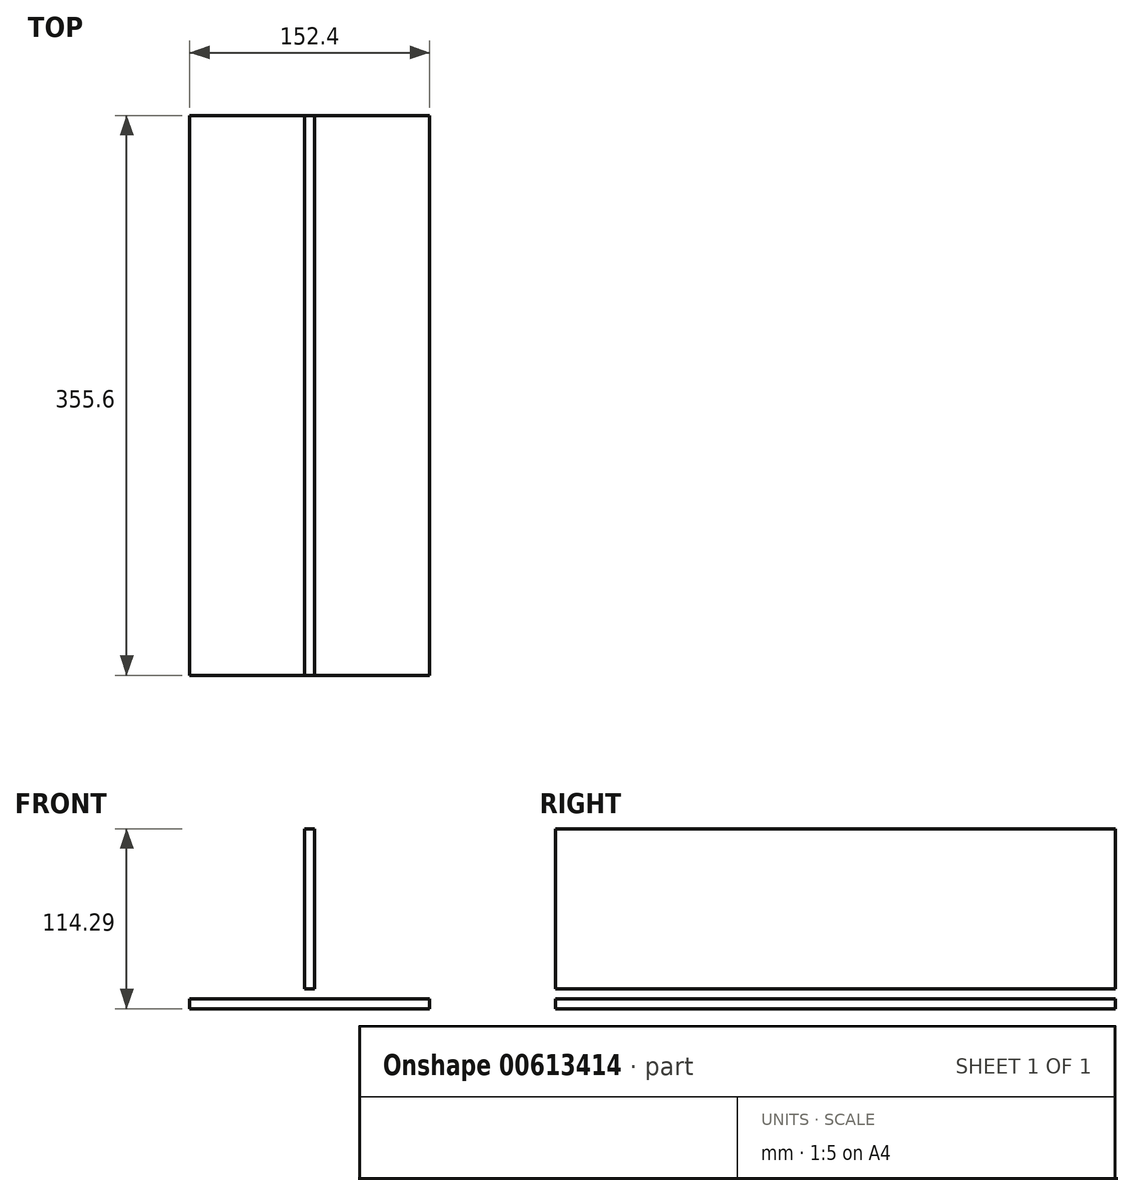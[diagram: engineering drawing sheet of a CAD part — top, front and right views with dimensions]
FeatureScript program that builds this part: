
annotation { "Feature Type Name" : "Feature", "Feature Type Description" : "" }
export const myFeature = defineFeature(function(context is Context, id is Id, definition is map)
    precondition{}
    {
        {
            var Q0;
            Q0=qCreatedBy(makeId("Front.planeOp"),FACE);
            var sketch = newSketch(context, id + "F0", { "sketchPlane" : qUnion([Q0])});
            skLineSegment(sketch, "E0.bottom", {"start": v(-76.2, 3.17) * mm, "end": v(76.2, 3.17) * mm});
            skLineSegment(sketch, "E0.top", {"start": v(-76.2, -3.17) * mm, "end": v(76.2, -3.17) * mm});
            skLineSegment(sketch, "E0.left", {"start": v(-76.2, 3.17) * mm, "end": v(-76.2, -3.17) * mm});
            skLineSegment(sketch, "E0.right", {"start": v(76.2, 3.17) * mm, "end": v(76.2, -3.17) * mm});
            skPoint(sketch, "E0.middle", {"position": v(0, 0) * mm});
            skSolve(sketch);
        }
        {
            var Q0;
            Q0=makeQuery(id+"F0.imprint","IMPRINT",FACE,{"disambiguationData":[TD([[makeQuery(id+"F0.imprint","IMPRINT",EDGE,{"derivedFrom":sQuery(id+"F0.wireOp",EDGE,"E0.bottom")}),-1.0]])]});
            extrude(context, id + "F1", {"entities" : qUnion([Q0]), "depth" : 355.6 * mm, "offsetDistance" : 25.4 * mm});
        }
        {
            var Q0;
            Q0=qCreatedBy(makeId("Front.planeOp"),FACE);
            var sketch = newSketch(context, id + "F2", { "sketchPlane" : qUnion([Q0])});
            skLineSegment(sketch, "E1.bottom", {"start": v(-3.17, 9.52) * mm, "end": v(3.18, 9.52) * mm});
            skLineSegment(sketch, "E1.top", {"start": v(-3.18, 111.12) * mm, "end": v(3.17, 111.12) * mm});
            skLineSegment(sketch, "E1.left", {"start": v(-3.17, 9.52) * mm, "end": v(-3.18, 111.12) * mm});
            skLineSegment(sketch, "E1.right", {"start": v(3.18, 9.52) * mm, "end": v(3.17, 111.12) * mm});
            skSolve(sketch);
        }
        {
            var Q0;
            Q0=makeQuery(id+"F2.imprint","IMPRINT",FACE,{"disambiguationData":[TD([[makeQuery(id+"F2.imprint","IMPRINT",EDGE,{"derivedFrom":sQuery(id+"F2.wireOp",EDGE,"E1.bottom")}),1.0]])]});
            extrude(context, id + "F3", {"entities" : qUnion([Q0]), "depth" : 355.6 * mm, "offsetDistance" : 25.4 * mm});
        }
    });
